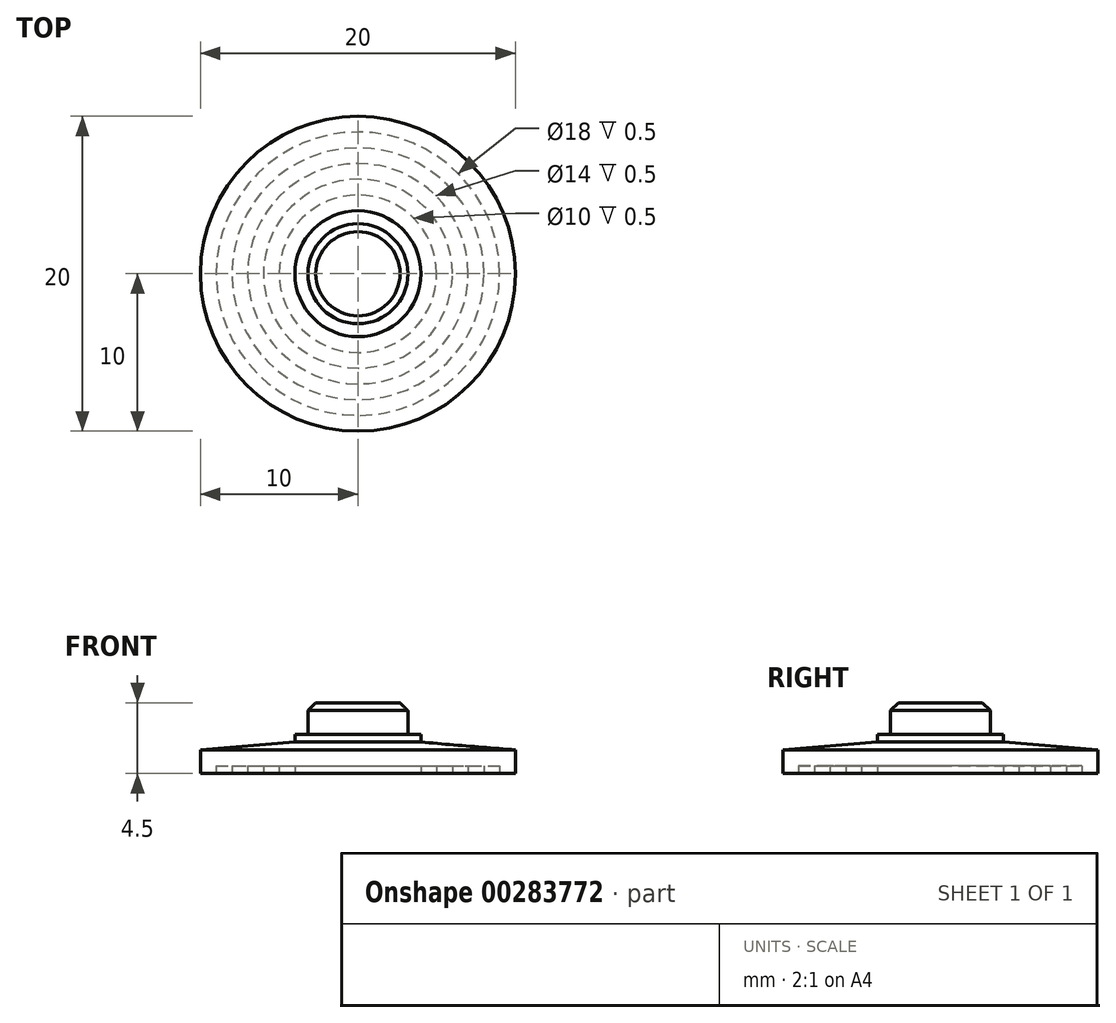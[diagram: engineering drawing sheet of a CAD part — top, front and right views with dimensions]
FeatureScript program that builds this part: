
annotation { "Feature Type Name" : "Feature", "Feature Type Description" : "" }
export const myFeature = defineFeature(function(context is Context, id is Id, definition is map)
    precondition{}
    {
        {
            var Q0;
            Q0=qCreatedBy(makeId("Top.planeOp"),FACE);
            var sketch = newSketch(context, id + "F0", { "sketchPlane" : qUnion([Q0])});
            skCircle(sketch, "E0", {"center": v(0, 0) * mm, "radius": 10 * mm});
            skSolve(sketch);
        }
        {
            var Q0;
            Q0=makeQuery(id+"F0.imprint","IMPRINT",FACE,{"disambiguationData":[TD([[makeQuery(id+"F0.imprint","IMPRINT",EDGE,{"derivedFrom":sQuery(id+"F0.wireOp",EDGE,"E0")}),1.0]])]});
            extrude(context, id + "F1", {"entities" : qUnion([Q0]), "depth" : 2 * mm, "offsetDistance" : 25 * mm});
        }
        {
            var Q0;
            Q0=makeQuery(id+"F1.opExtrude","CAP_FACE",FACE,{"disambiguationData":[OSD([sQuery(id+"F0.wireOp",EDGE,"E0")])],"isStart":false});
            var sketch = newSketch(context, id + "F2", { "sketchPlane" : qUnion([Q0])});
            skCircle(sketch, "E1", {"center": v(0, 0) * mm, "radius": 4 * mm});
            skSolve(sketch);
        }
        {
            var Q0;
            Q0=makeQuery(id+"F2.imprint","IMPRINT",FACE,{"disambiguationData":[TD([[makeQuery(id+"F2.imprint","IMPRINT",EDGE,{"derivedFrom":sQuery(id+"F2.wireOp",EDGE,"E1")}),1.0]])]});
            extrude(context, id + "F3", {"entities" : qUnion([Q0]), "operationType" : NewBodyOperationType.ADD, "depth" : .5 * mm, "offsetDistance" : 25 * mm});
        }
        {
            var Q0;
            Q0=makeQuery(id+"F3.opExtrude","CAP_FACE",FACE,{"disambiguationData":[OSD([sQuery(id+"F2.wireOp",EDGE,"E1")])],"isStart":false});
            var sketch = newSketch(context, id + "F4", { "sketchPlane" : qUnion([Q0])});
            skCircle(sketch, "E2", {"center": v(0, 0) * mm, "radius": 3.18 * mm});
            skSolve(sketch);
        }
        {
            var Q0;
            Q0=makeQuery(id+"F4.imprint","IMPRINT",FACE,{"disambiguationData":[TD([[makeQuery(id+"F4.imprint","IMPRINT",EDGE,{"derivedFrom":sQuery(id+"F4.wireOp",EDGE,"E2")}),1.0]])]});
            extrude(context, id + "F5", {"entities" : qUnion([Q0]), "operationType" : NewBodyOperationType.ADD, "depth" : 2 * mm, "offsetDistance" : 25 * mm});
        }
        {
            var Q0;
            Q0=makeQuery(id+"F1.opExtrude","CAP_FACE",FACE,{"disambiguationData":[OSD([sQuery(id+"F0.wireOp",EDGE,"E0")])],"isStart":true});
            var sketch = newSketch(context, id + "F6", { "sketchPlane" : qUnion([Q0])});
            skCircle(sketch, "E3", {"center": v(0, 0) * mm, "radius": 9 * mm});
            skCircle(sketch, "E4", {"center": v(0, 0) * mm, "radius": 8 * mm});
            skCircle(sketch, "E5", {"center": v(0, 0) * mm, "radius": 6 * mm});
            skCircle(sketch, "E6", {"center": v(0, 0) * mm, "radius": 5 * mm});
            skCircle(sketch, "E7", {"center": v(0, 0) * mm, "radius": 7 * mm});
            skCircle(sketch, "E8", {"center": v(0, 0) * mm, "radius": 4 * mm});
            skSolve(sketch);
        }
        {
            var Q0;
            Q0=makeQuery(id+"F6.imprint","IMPRINT",FACE,{"disambiguationData":[TD([[makeQuery(id+"F6.imprint","IMPRINT",EDGE,{"derivedFrom":sQuery(id+"F6.wireOp",EDGE,"E3")}),1.0]])]});
            var Q1;
            Q1=makeQuery(id+"F6.imprint","IMPRINT",FACE,{"disambiguationData":[TD([[makeQuery(id+"F6.imprint","IMPRINT",EDGE,{"derivedFrom":sQuery(id+"F6.wireOp",EDGE,"E5")}),-1.0]])]});
            var Q2;
            Q2=makeQuery(id+"F6.imprint","IMPRINT",FACE,{"disambiguationData":[TD([[makeQuery(id+"F6.imprint","IMPRINT",EDGE,{"derivedFrom":sQuery(id+"F6.wireOp",EDGE,"E6")}),1.0]])]});
            extrude(context, id + "F7", {"entities" : qUnion([Q0, Q1, Q2]), "operationType" : NewBodyOperationType.REMOVE, "oppositeDirection" : true, "depth" : .5 * mm, "offsetDistance" : 25 * mm});
        }
        {
            var Q0;
            Q0=makeQuery(id+"F1.opExtrude","CAP_EDGE",EDGE,{"disambiguationData":[OSD([sQuery(id+"F0.wireOp",EDGE,"E0")])],"isStart":false});
            chamfer(context, id + "F8", {"entities" : qUnion([Q0]), "chamferType" : ChamferType.TWO_OFFSETS, "width1" : 6 * mm, "oppositeDirection" : false, "width2" : .5 * mm, "tangentPropagation" : true});
        }
        {
            var Q0;
            Q0=makeQuery(id+"F5.opExtrude","CAP_EDGE",EDGE,{"disambiguationData":[OSD([sQuery(id+"F4.wireOp",EDGE,"E2")])],"isStart":false});
            chamfer(context, id + "F9", {"entities" : qUnion([Q0]), "width" : .5 * mm, "tangentPropagation" : true});
        }
    });
